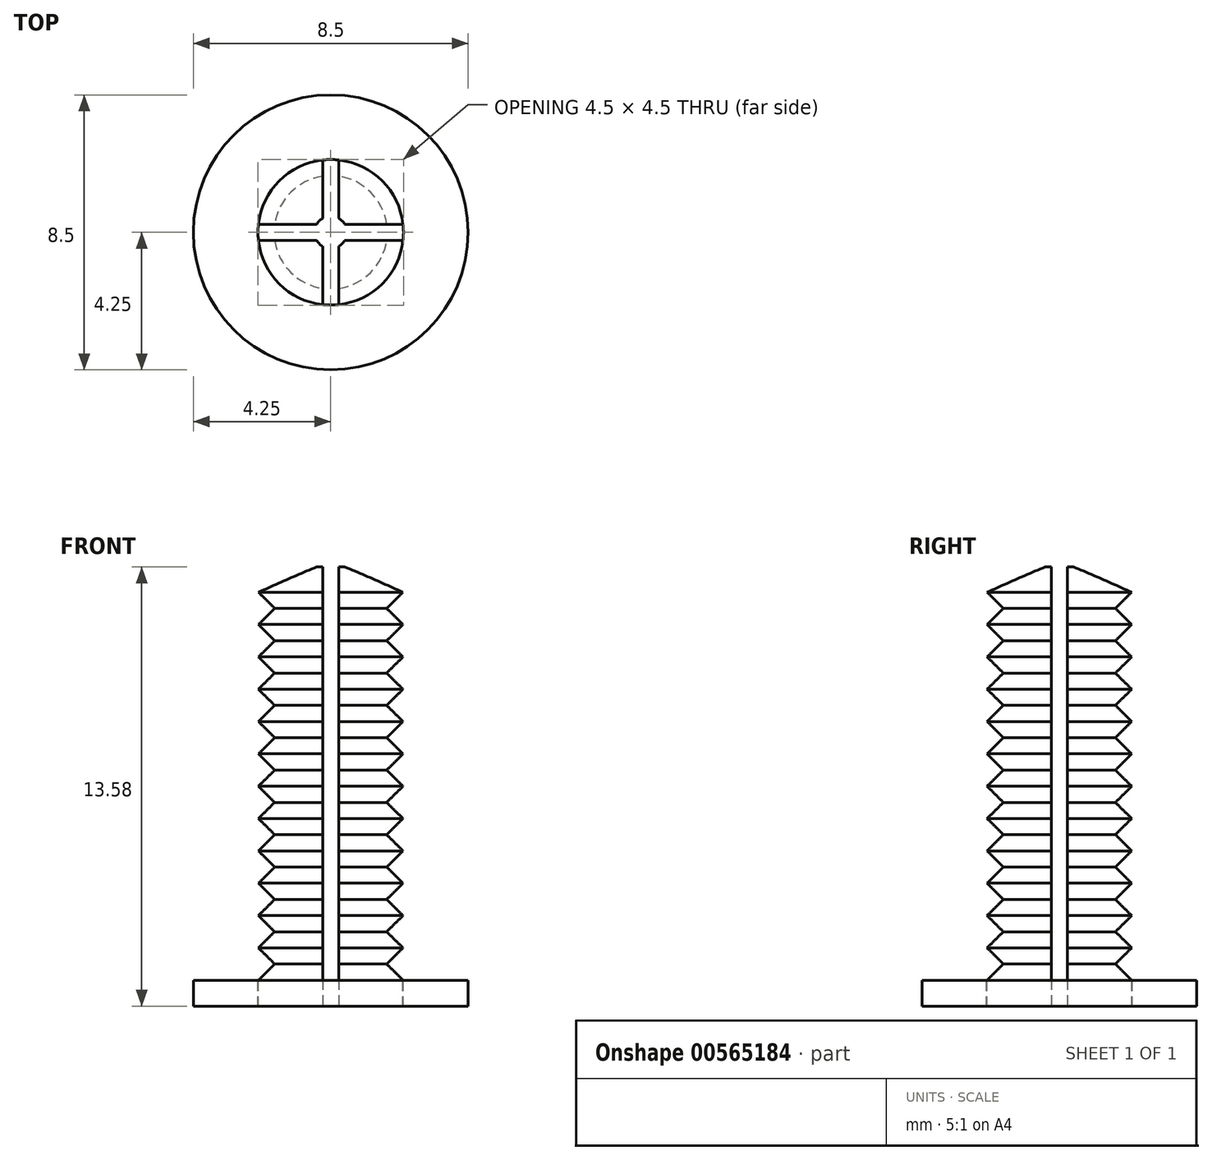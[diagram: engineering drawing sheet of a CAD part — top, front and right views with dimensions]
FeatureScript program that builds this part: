
annotation { "Feature Type Name" : "Feature", "Feature Type Description" : "" }
export const myFeature = defineFeature(function(context is Context, id is Id, definition is map)
    precondition{}
    {
        {
            assignVariable(context, id + "F0", {"name" : "T", "anyValue" : 0.8});
        }
        {
            var Q0;
            Q0=qCreatedBy(makeId("Top.planeOp"),FACE);
            var sketch = newSketch(context, id + "F1", { "sketchPlane" : qUnion([Q0])});
            skCircle(sketch, "E0", {"center": v(0, 0) * mm, "radius": 4.25 * mm});
            skCircle(sketch, "E1", {"center": v(0, 0) * mm, "radius": 2.25 * mm});
            skCircle(sketch, "E2", {"center": v(0, 0) * mm, "radius": 0.5 * mm});
            skLineSegment(sketch, "E3", {"start": v(-0.25, -0.43) * mm, "end": v(-0.25, -2.24) * mm});
            skLineSegment(sketch, "E4", {"start": v(0.25, -0.43) * mm, "end": v(0.25, -2.24) * mm});
            skLineSegment(sketch, "E5.1.0", {"start": v(0.43, 0.25) * mm, "end": v(2.24, 0.25) * mm});
            skLineSegment(sketch, "E5.1.1", {"start": v(0.43, -0.25) * mm, "end": v(2.24, -0.25) * mm});
            skLineSegment(sketch, "E5.2.0", {"start": v(-0.25, 0.43) * mm, "end": v(-0.25, 2.24) * mm});
            skLineSegment(sketch, "E5.2.1", {"start": v(0.25, 0.43) * mm, "end": v(0.25, 2.24) * mm});
            skLineSegment(sketch, "E5.3.0", {"start": v(-0.43, -0.25) * mm, "end": v(-2.24, -0.25) * mm});
            skLineSegment(sketch, "E5.3.1", {"start": v(-0.43, 0.25) * mm, "end": v(-2.24, 0.25) * mm});
            skSolve(sketch);
        }
        {
            var Q0;
            Q0=qCreatedBy(makeId("Front.planeOp"),FACE);
            var sketch = newSketch(context, id + "F2", { "sketchPlane" : qUnion([Q0])});
            skLineSegment(sketch, "E6.0", {"start": v(-2.25, 0) * mm, "end": v(2.25, 0) * mm});
            skLineSegment(sketch, "E7", {"start": v(-2.25, 0) * mm, "end": v(-1.75, 0.5) * mm});
            skLineSegment(sketch, "E8", {"start": v(-1.75, 0.5) * mm, "end": v(-2.25, 1) * mm});
            skLineSegment(sketch, "E9", {"start": v(0, 0) * mm, "end": v(0, 13) * mm});
            skLineSegment(sketch, "E10.0.1.0", {"start": v(-1.75, 1.5) * mm, "end": v(-2.25, 2) * mm});
            skLineSegment(sketch, "E10.0.1.1", {"start": v(-2.25, 1) * mm, "end": v(-1.75, 1.5) * mm});
            skLineSegment(sketch, "E10.0.2.0", {"start": v(-1.75, 2.5) * mm, "end": v(-2.25, 3) * mm});
            skLineSegment(sketch, "E10.0.2.1", {"start": v(-2.25, 2) * mm, "end": v(-1.75, 2.5) * mm});
            skLineSegment(sketch, "E10.0.3.0", {"start": v(-1.75, 3.5) * mm, "end": v(-2.25, 4) * mm});
            skLineSegment(sketch, "E10.0.3.1", {"start": v(-2.25, 3) * mm, "end": v(-1.75, 3.5) * mm});
            skLineSegment(sketch, "E10.0.4.0", {"start": v(-1.75, 4.5) * mm, "end": v(-2.25, 5) * mm});
            skLineSegment(sketch, "E10.0.4.1", {"start": v(-2.25, 4) * mm, "end": v(-1.75, 4.5) * mm});
            skLineSegment(sketch, "E10.0.5.0", {"start": v(-1.75, 5.5) * mm, "end": v(-2.25, 6) * mm});
            skLineSegment(sketch, "E10.0.5.1", {"start": v(-2.25, 5) * mm, "end": v(-1.75, 5.5) * mm});
            skLineSegment(sketch, "E10.0.6.0", {"start": v(-1.75, 6.5) * mm, "end": v(-2.25, 7) * mm});
            skLineSegment(sketch, "E10.0.6.1", {"start": v(-2.25, 6) * mm, "end": v(-1.75, 6.5) * mm});
            skLineSegment(sketch, "E10.0.7.0", {"start": v(-1.75, 7.5) * mm, "end": v(-2.25, 8) * mm});
            skLineSegment(sketch, "E10.0.7.1", {"start": v(-2.25, 7) * mm, "end": v(-1.75, 7.5) * mm});
            skLineSegment(sketch, "E10.0.8.0", {"start": v(-1.75, 8.5) * mm, "end": v(-2.25, 9) * mm});
            skLineSegment(sketch, "E10.0.8.1", {"start": v(-2.25, 8) * mm, "end": v(-1.75, 8.5) * mm});
            skLineSegment(sketch, "E10.0.9.0", {"start": v(-1.75, 9.5) * mm, "end": v(-2.25, 10) * mm});
            skLineSegment(sketch, "E10.0.9.1", {"start": v(-2.25, 9) * mm, "end": v(-1.75, 9.5) * mm});
            skLineSegment(sketch, "E10.0.10.0", {"start": v(-1.75, 10.5) * mm, "end": v(-2.25, 11) * mm});
            skLineSegment(sketch, "E10.0.10.1", {"start": v(-2.25, 10) * mm, "end": v(-1.75, 10.5) * mm});
            skLineSegment(sketch, "E10.0.11.0", {"start": v(-1.75, 11.5) * mm, "end": v(-2.25, 12) * mm});
            skLineSegment(sketch, "E10.0.11.1", {"start": v(-2.25, 11) * mm, "end": v(-1.75, 11.5) * mm});
            skLineSegment(sketch, "E10.direction1", {"start": v(-2.25, 0) * mm, "end": v(22.75, 0) * mm, "construction": true});
            skLineSegment(sketch, "E10.direction2", {"start": v(-2.25, 0) * mm, "end": v(-2.25, 1) * mm, "construction": true});
            skLineSegment(sketch, "E11", {"start": v(-2.25, 12) * mm, "end": v(0, 13) * mm});
            skSolve(sketch);
        }
        {
            var Q0;
            {var subQ1=sQuery(id+"F2.wireOp",EDGE,"E7");Q0=makeQuery(id+"F2.imprint","IMPRINT",FACE,{"disambiguationData":[TD([[makeQuery(id+"F2.imprint","IMPRINT",EDGE,{"derivedFrom":subQ1}),-1.0]])]});}
            var Q1;
            Q1=sQuery(id+"F2.wireOp",EDGE,"E9");
            revolve(context, id + "F3", {"entities" : qUnion([Q0]), "axis" : qUnion([Q1]), "revolveType" : RevolveType.FULL});
        }
        {
            var Q0;
            {var subQ0=sQuery(id+"F1.wireOp",EDGE,"E5.2.0");Q0=makeQuery(id+"F1.imprint","IMPRINT",FACE,{"disambiguationData":[TD([[makeQuery(id+"F1.imprint","IMPRINT",EDGE,{"derivedFrom":subQ0}),1.0]])]});}
            var Q1;
            {var subQ0=sQuery(id+"F1.wireOp",EDGE,"E5.1.0");Q1=makeQuery(id+"F1.imprint","IMPRINT",FACE,{"disambiguationData":[TD([[makeQuery(id+"F1.imprint","IMPRINT",EDGE,{"derivedFrom":subQ0}),1.0]])]});}
            var Q2;
            Q2=makeQuery(id+"F1.imprint","IMPRINT",FACE,{"disambiguationData":[TD([[makeQuery(id+"F1.imprint","IMPRINT",EDGE,{"derivedFrom":sQuery(id+"F1.wireOp",EDGE,"E0")}),1.0]])]});
            var Q3;
            {var subQ0=sQuery(id+"F1.wireOp",EDGE,"E3");Q3=makeQuery(id+"F1.imprint","IMPRINT",FACE,{"disambiguationData":[TD([[makeQuery(id+"F1.imprint","IMPRINT",EDGE,{"derivedFrom":subQ0}),-1.0]])]});}
            var Q4;
            {var subQ0=sQuery(id+"F1.wireOp",EDGE,"E5.3.0");Q4=makeQuery(id+"F1.imprint","IMPRINT",FACE,{"disambiguationData":[TD([[makeQuery(id+"F1.imprint","IMPRINT",EDGE,{"derivedFrom":subQ0}),-1.0]])]});}
            var Q5;
            {var subQ0=sQuery(id+"F1.wireOp",EDGE,"E5.1.0");Q5=makeQuery(id+"F1.imprint","IMPRINT",FACE,{"disambiguationData":[TD([[makeQuery(id+"F1.imprint","IMPRINT",EDGE,{"derivedFrom":subQ0}),-1.0]])]});}
            var Q6;
            {var subQ0=sQuery(id+"F1.wireOp",EDGE,"E3");Q6=makeQuery(id+"F1.imprint","IMPRINT",FACE,{"disambiguationData":[TD([[makeQuery(id+"F1.imprint","IMPRINT",EDGE,{"derivedFrom":subQ0}),1.0]])]});}
            var Q7;
            {var subQ0=sQuery(id+"F1.wireOp",EDGE,"E4");Q7=makeQuery(id+"F1.imprint","IMPRINT",FACE,{"disambiguationData":[TD([[makeQuery(id+"F1.imprint","IMPRINT",EDGE,{"derivedFrom":subQ0}),1.0]])]});}
            var Q8;
            {var subQ0=sQuery(id+"F1.wireOp",EDGE,"E5.2.0");Q8=makeQuery(id+"F1.imprint","IMPRINT",FACE,{"disambiguationData":[TD([[makeQuery(id+"F1.imprint","IMPRINT",EDGE,{"derivedFrom":subQ0}),-1.0]])]});}
            extrude(context, id + "F4", {"entities" : qUnion([Q0, Q1, Q2, Q3, Q4, Q5, Q6, Q7, Q8]), "operationType" : NewBodyOperationType.ADD, "oppositeDirection" : true, "depth" : getVariable(context, 'T') * mm, "offsetDistance" : 25 * mm});
        }
        {
            var Q0;
            Q0=makeQuery(id+"F1.imprint","IMPRINT",FACE,{"disambiguationData":[TD([[makeQuery(id+"F1.imprint","IMPRINT",EDGE,{"derivedFrom":sQuery(id+"F1.wireOp",EDGE,"E2")}),1.0]])]});
            var Q1;
            {var subQ0=sQuery(id+"F1.wireOp",EDGE,"E5.3.0");Q1=makeQuery(id+"F1.imprint","IMPRINT",FACE,{"disambiguationData":[TD([[makeQuery(id+"F1.imprint","IMPRINT",EDGE,{"derivedFrom":subQ0}),-1.0]])]});}
            var Q2;
            {var subQ0=sQuery(id+"F1.wireOp",EDGE,"E5.2.0");Q2=makeQuery(id+"F1.imprint","IMPRINT",FACE,{"disambiguationData":[TD([[makeQuery(id+"F1.imprint","IMPRINT",EDGE,{"derivedFrom":subQ0}),-1.0]])]});}
            var Q3;
            {var subQ0=sQuery(id+"F1.wireOp",EDGE,"E5.1.0");Q3=makeQuery(id+"F1.imprint","IMPRINT",FACE,{"disambiguationData":[TD([[makeQuery(id+"F1.imprint","IMPRINT",EDGE,{"derivedFrom":subQ0}),-1.0]])]});}
            var Q4;
            {var subQ0=sQuery(id+"F1.wireOp",EDGE,"E3");Q4=makeQuery(id+"F1.imprint","IMPRINT",FACE,{"disambiguationData":[TD([[makeQuery(id+"F1.imprint","IMPRINT",EDGE,{"derivedFrom":subQ0}),1.0]])]});}
            extrude(context, id + "F5", {"entities" : qUnion([Q0, Q1, Q2, Q3, Q4]), "operationType" : NewBodyOperationType.REMOVE, "endBound" : BoundingType.THROUGH_ALL, "depth" : 25 * mm, "offsetDistance" : 25 * mm});
        }
        {
            var Q0;
            {var subQ0=sQuery(id+"F1.wireOp",EDGE,"E5.3.0");Q0=makeQuery(id+"F1.imprint","IMPRINT",FACE,{"disambiguationData":[TD([[makeQuery(id+"F1.imprint","IMPRINT",EDGE,{"derivedFrom":subQ0}),-1.0]])]});}
            var Q1;
            {var subQ0=sQuery(id+"F1.wireOp",EDGE,"E3");Q1=makeQuery(id+"F1.imprint","IMPRINT",FACE,{"disambiguationData":[TD([[makeQuery(id+"F1.imprint","IMPRINT",EDGE,{"derivedFrom":subQ0}),1.0]])]});}
            var Q2;
            {var subQ0=sQuery(id+"F1.wireOp",EDGE,"E5.1.0");Q2=makeQuery(id+"F1.imprint","IMPRINT",FACE,{"disambiguationData":[TD([[makeQuery(id+"F1.imprint","IMPRINT",EDGE,{"derivedFrom":subQ0}),-1.0]])]});}
            var Q3;
            {var subQ0=sQuery(id+"F1.wireOp",EDGE,"E5.2.0");Q3=makeQuery(id+"F1.imprint","IMPRINT",FACE,{"disambiguationData":[TD([[makeQuery(id+"F1.imprint","IMPRINT",EDGE,{"derivedFrom":subQ0}),-1.0]])]});}
            extrude(context, id + "F6", {"entities" : qUnion([Q0, Q1, Q2, Q3]), "operationType" : NewBodyOperationType.REMOVE, "oppositeDirection" : true, "depth" : 25 * mm, "offsetDistance" : 25 * mm});
        }
    });
